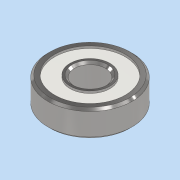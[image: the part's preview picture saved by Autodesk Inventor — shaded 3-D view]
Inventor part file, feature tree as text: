
AUTODESK INVENTOR PART (.ipt)
format: ipt  version: 2021.2 (Build 252289000, 289)  size: 144,384 bytes
history: native  units: mm
features: other x2, extrude x2, sketch x1, chamfer x1
ambient origin geometry x8: Origin, YZ Plane, XZ Plane, XY Plane, X Axis, Y Axis, Z Axis, Center Point
bodies: Body1 (feature_tree)
feature tree (6):
  other  "<userpath>\Desktop\Daniil\MIET\PID_controller\Mechanics\3D_model\PID_demensions.xlsx"
  other  "Твердое тело1"
  sketch  "Эскиз1"
  extrude  "Выдавливание1"  Depth=19.0mm
  extrude  "Выдавливание2"  Depth=7.0mm
  chamfer  "Фаска1"  Distance=1.5mm
